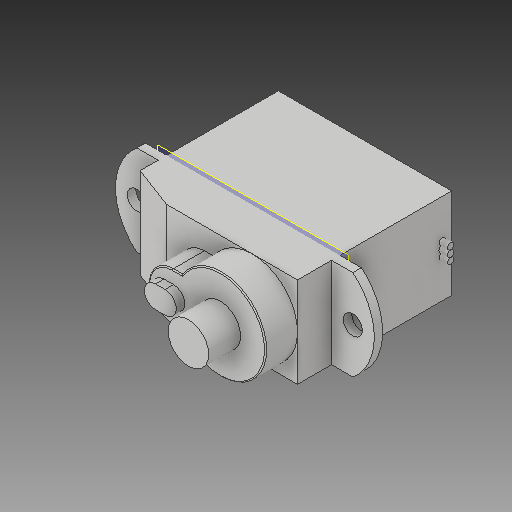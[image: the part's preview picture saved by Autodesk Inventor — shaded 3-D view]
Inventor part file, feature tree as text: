
AUTODESK INVENTOR PART (.ipt)
format: ipt  version: 2018 (Build 220112000, 112)  size: 213,504 bytes
history: native  units: mm
features: sketch x7, extrude x6, other x2, mirror x1, chamfer x1, fillet x1
ambient origin geometry x8: Origin, YZ Plane, XZ Plane, XY Plane, X Axis, Y Axis, Z Axis, Center Point
bodies: Body1 (feature_tree)
feature tree (18):
  other  "ソリッド1"
  extrude  "押し出し1"  Depth=16.3mm
  other  "作業平面2"
  extrude  "押し出し3"  Depth=8.5mm
  mirror  "ミラー1"
  extrude  "押し出し4"  Depth=14.5mm TaperAngle=0.0deg
  chamfer  "面取り1"  [1 undecoded]
  sketch  "スケッチ5"
  extrude  "押し出し5"  Depth=1.8mm
  extrude  "押し出し6"  Depth=2.0mm
  extrude  "押し出し7"  Depth=5.5mm
  fillet  "フィレット1"  Radius=0.8mm
  sketch  "スケッチ1"
  sketch  "スケッチ3"
  sketch  "スケッチ4"
  sketch  "スケッチ6"
  sketch  "スケッチ7"
  sketch  "スケッチ8"
note: 1 required parameter value undecoded (feature->parameter linkage not recoverable at this tier; creation-order binding heuristic only, values carry confidence <= 0.55)
